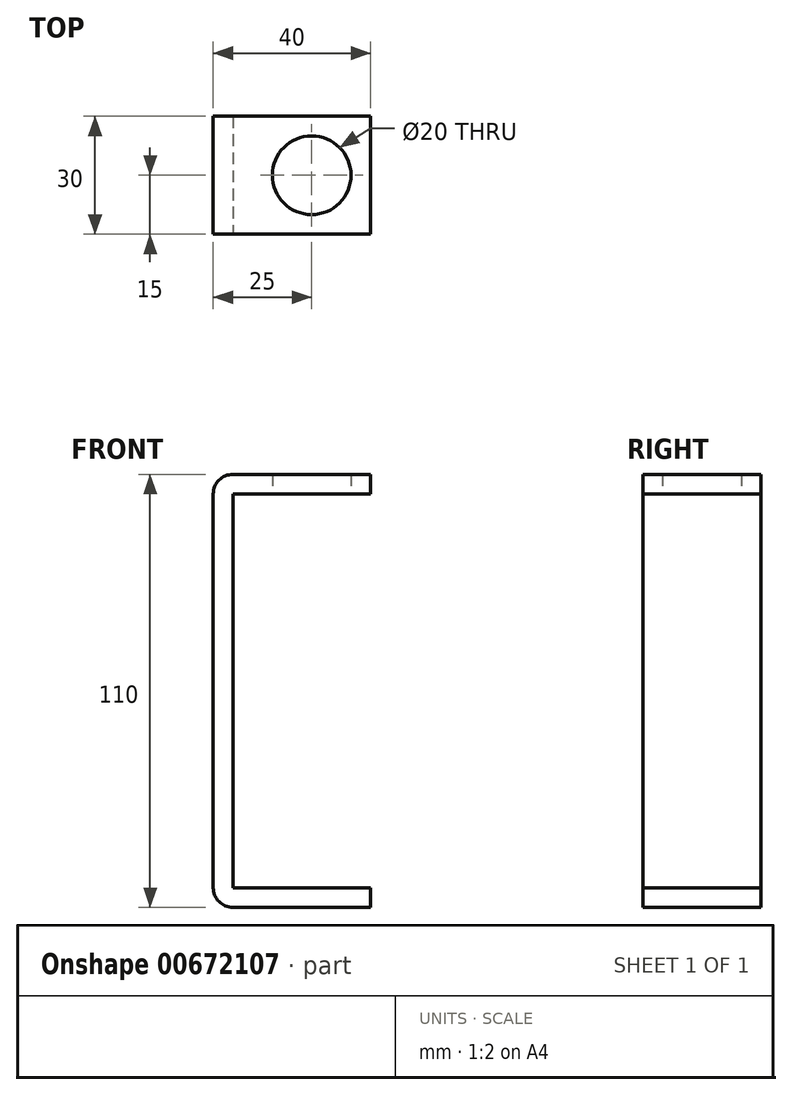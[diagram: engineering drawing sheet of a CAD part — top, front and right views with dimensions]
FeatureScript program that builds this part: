
annotation { "Feature Type Name" : "Feature", "Feature Type Description" : "" }
export const myFeature = defineFeature(function(context is Context, id is Id, definition is map)
    precondition{}
    {
        {
            var Q0;
            Q0=qCreatedBy(makeId("Top.planeOp"),FACE);
            var sketch = newSketch(context, id + "F0", { "sketchPlane" : qUnion([Q0])});
            skLineSegment(sketch, "E0.bottom", {"start": v(-20, 15) * mm, "end": v(20, 15) * mm});
            skLineSegment(sketch, "E0.top", {"start": v(-20, -15) * mm, "end": v(20, -15) * mm});
            skLineSegment(sketch, "E0.left", {"start": v(-20, 15) * mm, "end": v(-20, -15) * mm});
            skLineSegment(sketch, "E0.right", {"start": v(20, 15) * mm, "end": v(20, -15) * mm});
            skLineSegment(sketch, "E1", {"start": v(-15, 15) * mm, "end": v(-15, -15) * mm});
            skSolve(sketch);
        }
        {
            var Q0;
            Q0 = qSketchRegion(id + "F0", true);
            extrude(context, id + "F1", {"entities" : qUnion([Q0]), "oppositeDirection" : true, "depth" : 5 * mm, "offsetDistance" : 25 * mm});
        }
        {
            var Q0;
            {var subQ0=sQuery(id+"F0.wireOp",EDGE,"E0.left");Q0=makeQuery(id+"F0.imprint","IMPRINT",FACE,{"disambiguationData":[TD([[makeQuery(id+"F0.imprint","IMPRINT",EDGE,{"derivedFrom":subQ0}),1.0]])]});}
            extrude(context, id + "F2", {"entities" : qUnion([Q0]), "operationType" : NewBodyOperationType.ADD, "depth" : 100 * mm, "offsetDistance" : 25 * mm});
        }
        {
            var Q0;
            Q0=makeQuery(id+"F2.opExtrude","CAP_FACE",FACE,{"disambiguationData":[OSD([sQuery(id+"F0.wireOp",EDGE,"E0.bottom"),sQuery(id+"F0.wireOp",EDGE,"E0.top"),sQuery(id+"F0.wireOp",EDGE,"E0.left"),sQuery(id+"F0.wireOp",EDGE,"E1")])],"isStart":false});
            var sketch = newSketch(context, id + "F3", { "sketchPlane" : qUnion([Q0])});
            skLineSegment(sketch, "E2.bottom", {"start": v(-20, 15) * mm, "end": v(20, 15) * mm});
            skLineSegment(sketch, "E2.top", {"start": v(-20, -15) * mm, "end": v(20, -15) * mm});
            skLineSegment(sketch, "E2.left", {"start": v(-20, 15) * mm, "end": v(-20, -15) * mm});
            skLineSegment(sketch, "E2.right", {"start": v(20, 15) * mm, "end": v(20, -15) * mm});
            skCircle(sketch, "E3", {"center": v(5, 0) * mm, "radius": 10 * mm});
            skSolve(sketch);
        }
        {
            var Q0;
            Q0 = qSketchRegion(id + "F3", true);
            extrude(context, id + "F4", {"entities" : qUnion([Q0]), "operationType" : NewBodyOperationType.ADD, "depth" : 5 * mm, "offsetDistance" : 25 * mm});
        }
        {
            var Q0;
            Q0=makeQuery(id+"F1.opExtrude","CAP_EDGE",EDGE,{"disambiguationData":[OSD([sQuery(id+"F0.wireOp",EDGE,"E0.left")])],"isStart":false});
            var Q1;
            Q1=makeQuery(id+"F4.opExtrude","CAP_EDGE",EDGE,{"disambiguationData":[OSD([sQuery(id+"F3.wireOp",EDGE,"E2.left")])],"isStart":false});
            fillet(context, id + "F5", {"entities" : qUnion([Q0, Q1]), "radius" : 5 * mm, "tangentPropagation" : true, "allowEdgeOverflow" : false});
        }
    });
